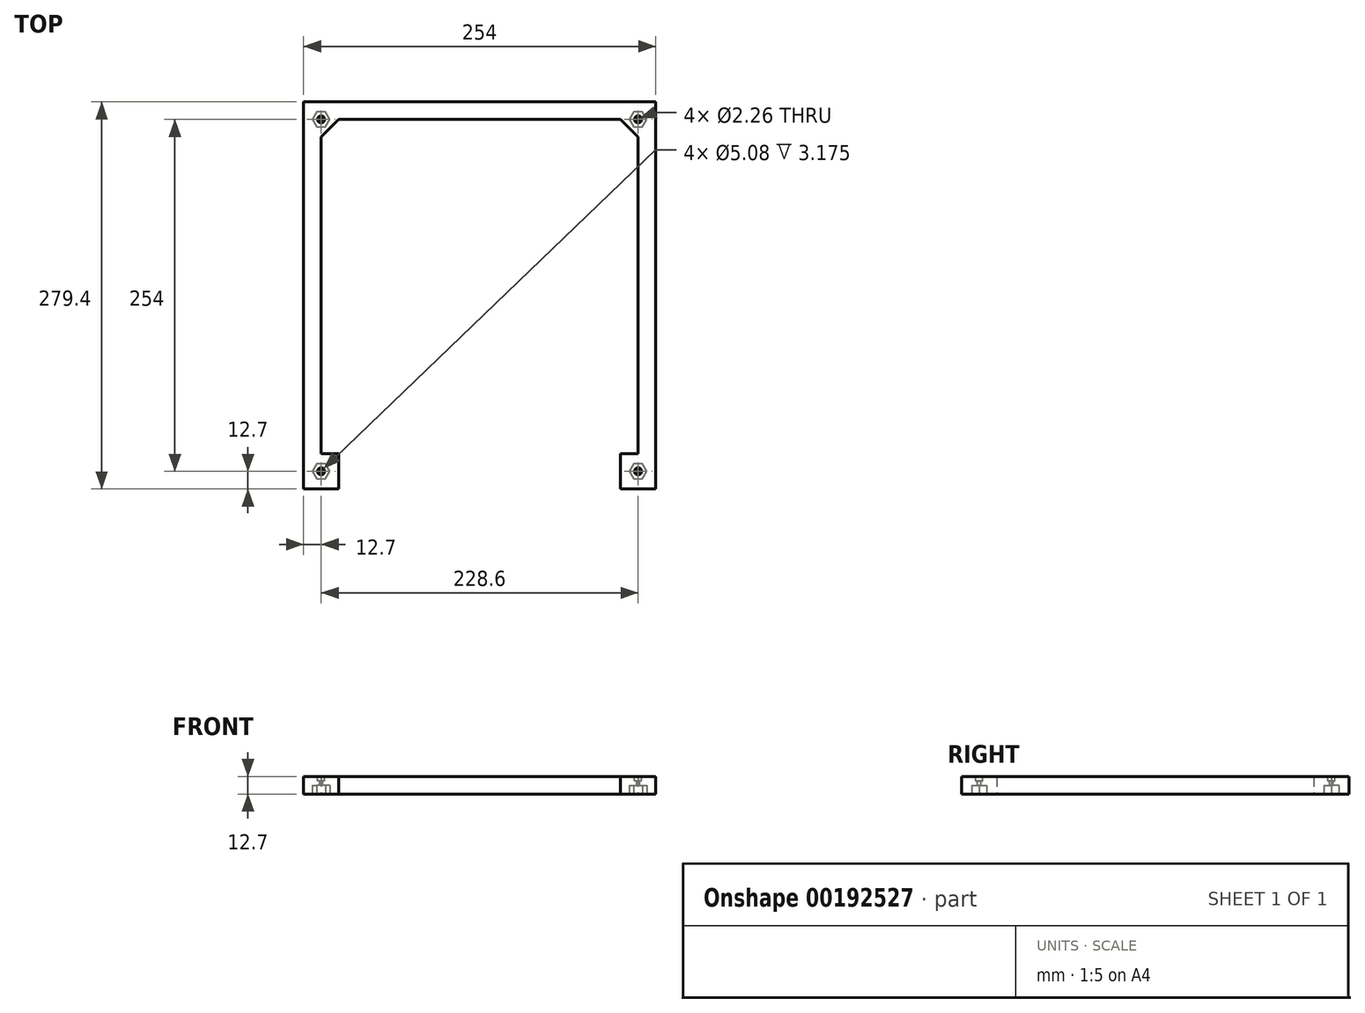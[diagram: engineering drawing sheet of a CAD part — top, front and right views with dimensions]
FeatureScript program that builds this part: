
annotation { "Feature Type Name" : "Feature", "Feature Type Description" : "" }
export const myFeature = defineFeature(function(context is Context, id is Id, definition is map)
    precondition{}
    {
        {
            var Q0;
            Q0=qCreatedBy(makeId("Top.planeOp"),FACE);
            var sketch = newSketch(context, id + "F0", { "sketchPlane" : qUnion([Q0])});
            skLineSegment(sketch, "E0.bottom", {"start": v(101.6, 127) * mm, "end": v(-101.6, 127) * mm});
            skLineSegment(sketch, "E0.left", {"start": v(114.3, 114.3) * mm, "end": v(114.3, -114.3) * mm});
            skLineSegment(sketch, "E0.right", {"start": v(-114.3, 114.3) * mm, "end": v(-114.3, -114.3) * mm});
            skPoint(sketch, "E0.middle", {"position": v(0, 0) * mm});
            skLineSegment(sketch, "E1.bottom", {"start": v(127, 139.7) * mm, "end": v(-127, 139.7) * mm});
            skLineSegment(sketch, "E1.top", {"start": v(127, -139.7) * mm, "end": v(114.3, -139.7) * mm});
            skLineSegment(sketch, "E1.left", {"start": v(127, 139.7) * mm, "end": v(127, -139.7) * mm});
            skLineSegment(sketch, "E1.right", {"start": v(-127, 139.7) * mm, "end": v(-127, -139.7) * mm});
            skLineSegment(sketch, "E2.trimOffspring", {"start": v(-114.3, -139.7) * mm, "end": v(-127, -139.7) * mm});
            skLineSegment(sketch, "E3.bottom", {"start": v(-127, 139.7) * mm, "end": v(-101.6, 139.7) * mm});
            skLineSegment(sketch, "E3.left", {"start": v(-127, 139.7) * mm, "end": v(-127, 114.3) * mm});
            skLineSegment(sketch, "E4.bottom", {"start": v(127, 139.7) * mm, "end": v(101.6, 139.7) * mm});
            skLineSegment(sketch, "E4.left", {"start": v(127, 139.7) * mm, "end": v(127, 114.3) * mm});
            skLineSegment(sketch, "E5.bottom", {"start": v(127, -139.7) * mm, "end": v(101.6, -139.7) * mm});
            skLineSegment(sketch, "E5.top", {"start": v(114.3, -114.3) * mm, "end": v(101.6, -114.3) * mm});
            skLineSegment(sketch, "E5.left", {"start": v(127, -139.7) * mm, "end": v(127, -114.3) * mm});
            skLineSegment(sketch, "E5.right", {"start": v(101.6, -139.7) * mm, "end": v(101.6, -114.3) * mm});
            skLineSegment(sketch, "E6.bottom", {"start": v(-127, -139.7) * mm, "end": v(-101.6, -139.7) * mm});
            skLineSegment(sketch, "E6.top", {"start": v(-114.3, -114.3) * mm, "end": v(-101.6, -114.3) * mm});
            skLineSegment(sketch, "E6.left", {"start": v(-127, -139.7) * mm, "end": v(-127, -114.3) * mm});
            skLineSegment(sketch, "E6.right", {"start": v(-101.6, -139.7) * mm, "end": v(-101.6, -114.3) * mm});
            skPoint(sketch, "E7.orphan", {"position": v(-114.3, 127) * mm});
            skPoint(sketch, "E8.start.orphan", {"position": v(-114.3, -127) * mm});
            skPoint(sketch, "E9.start.orphan", {"position": v(114.3, -127) * mm});
            skPoint(sketch, "E10.orphan", {"position": v(114.3, 127) * mm});
            skLineSegment(sketch, "E11", {"start": v(-114.3, 114.3) * mm, "end": v(-101.6, 127) * mm});
            skLineSegment(sketch, "E12", {"start": v(101.6, 127) * mm, "end": v(114.3, 114.3) * mm});
            skPoint(sketch, "E3.right.end.orphan", {"position": v(-101.6, 114.3) * mm});
            skPoint(sketch, "E4.top.end.orphan", {"position": v(101.6, 114.3) * mm});
            skSolve(sketch);
        }
        {
            var Q0;
            Q0 = qSketchRegion(id + "F0", true);
            extrude(context, id + "F1", {"entities" : qUnion([Q0]), "depth" : 12.7 * mm});
        }
        {
            var Q0;
            Q0=makeQuery(id+"F1.opExtrude","CAP_FACE",FACE,{"disambiguationData":[OSD([sQuery(id+"F0.wireOp",EDGE,"E0.bottom"),sQuery(id+"F0.wireOp",EDGE,"E0.left"),sQuery(id+"F0.wireOp",EDGE,"E0.right"),sQuery(id+"F0.wireOp",EDGE,"E1.bottom"),sQuery(id+"F0.wireOp",EDGE,"E1.left"),sQuery(id+"F0.wireOp",EDGE,"E1.right"),sQuery(id+"F0.wireOp",EDGE,"E3.bottom"),sQuery(id+"F0.wireOp",EDGE,"E3.top"),sQuery(id+"F0.wireOp",EDGE,"E3.left"),sQuery(id+"F0.wireOp",EDGE,"E3.right"),sQuery(id+"F0.wireOp",EDGE,"E4.bottom"),sQuery(id+"F0.wireOp",EDGE,"E4.top"),sQuery(id+"F0.wireOp",EDGE,"E4.left"),sQuery(id+"F0.wireOp",EDGE,"E4.right"),sQuery(id+"F0.wireOp",EDGE,"E5.bottom"),sQuery(id+"F0.wireOp",EDGE,"E5.top"),sQuery(id+"F0.wireOp",EDGE,"E5.left"),sQuery(id+"F0.wireOp",EDGE,"E5.right"),sQuery(id+"F0.wireOp",EDGE,"E6.bottom"),sQuery(id+"F0.wireOp",EDGE,"E6.top"),sQuery(id+"F0.wireOp",EDGE,"E6.left"),sQuery(id+"F0.wireOp",EDGE,"E6.right")])],"isStart":true});
            var sketch = newSketch(context, id + "F2", { "sketchPlane" : qUnion([Q0])});
            skSolve(sketch);
        }
        {
            var Q0;
            Q0=makeQuery(id+"F2.imprint","IMPRINT",FACE,{"disambiguationData":[TD([[makeQuery(id+"F2.imprint","IMPRINT",EDGE,{"derivedFrom":makeQuery(id+"F1.opExtrude","CAP_EDGE",EDGE,{"disambiguationData":[OSD([sQuery(id+"F0.wireOp",EDGE,"E0.bottom")])],"isStart":true})}),1.0]])]});
            var sketch = newSketch(context, id + "F3", { "sketchPlane" : qUnion([Q0])});
            skCircle(sketch, "E13.cCircle", {"center": v(-114.3, 127) * mm, "radius": 6.35 * mm, "construction": true});
            skLineSegment(sketch, "E13.0", {"start": v(-111.13, 121.5) * mm, "end": v(-117.48, 121.5) * mm});
            skLineSegment(sketch, "E13.1", {"start": v(-117.48, 121.5) * mm, "end": v(-120.65, 127) * mm});
            skLineSegment(sketch, "E13.2", {"start": v(-120.65, 127) * mm, "end": v(-117.48, 132.5) * mm});
            skLineSegment(sketch, "E13.3", {"start": v(-117.47, 132.5) * mm, "end": v(-111.12, 132.5) * mm});
            skLineSegment(sketch, "E13.4", {"start": v(-111.12, 132.5) * mm, "end": v(-107.95, 127) * mm});
            skLineSegment(sketch, "E13.5", {"start": v(-107.95, 127) * mm, "end": v(-111.13, 121.5) * mm});
            skCircle(sketch, "E14.cCircle", {"center": v(-114.3, -127) * mm, "radius": 6.35 * mm, "construction": true});
            skLineSegment(sketch, "E14.0", {"start": v(-111.12, -121.5) * mm, "end": v(-107.95, -127) * mm});
            skLineSegment(sketch, "E14.1", {"start": v(-107.95, -127) * mm, "end": v(-111.13, -132.5) * mm});
            skLineSegment(sketch, "E14.2", {"start": v(-111.13, -132.5) * mm, "end": v(-117.48, -132.5) * mm});
            skLineSegment(sketch, "E14.3", {"start": v(-117.48, -132.5) * mm, "end": v(-120.65, -127) * mm});
            skLineSegment(sketch, "E14.4", {"start": v(-120.65, -127) * mm, "end": v(-117.48, -121.5) * mm});
            skLineSegment(sketch, "E14.5", {"start": v(-117.48, -121.5) * mm, "end": v(-111.13, -121.5) * mm});
            skCircle(sketch, "E15.cCircle", {"center": v(114.3, -127) * mm, "radius": 6.35 * mm, "construction": true});
            skLineSegment(sketch, "E15.0", {"start": v(117.47, -121.5) * mm, "end": v(120.65, -127) * mm});
            skLineSegment(sketch, "E15.1", {"start": v(120.65, -127) * mm, "end": v(117.47, -132.5) * mm});
            skLineSegment(sketch, "E15.2", {"start": v(117.48, -132.5) * mm, "end": v(111.12, -132.5) * mm});
            skLineSegment(sketch, "E15.3", {"start": v(111.12, -132.5) * mm, "end": v(107.95, -127) * mm});
            skLineSegment(sketch, "E15.4", {"start": v(107.95, -127) * mm, "end": v(111.13, -121.5) * mm});
            skLineSegment(sketch, "E15.5", {"start": v(111.13, -121.5) * mm, "end": v(117.48, -121.5) * mm});
            skCircle(sketch, "E16.cCircle", {"center": v(114.3, 127) * mm, "radius": 6.35 * mm, "construction": true});
            skLineSegment(sketch, "E16.0", {"start": v(117.48, 132.5) * mm, "end": v(120.65, 127) * mm});
            skLineSegment(sketch, "E16.1", {"start": v(120.65, 127) * mm, "end": v(117.47, 121.5) * mm});
            skLineSegment(sketch, "E16.2", {"start": v(117.48, 121.5) * mm, "end": v(111.13, 121.5) * mm});
            skLineSegment(sketch, "E16.3", {"start": v(111.12, 121.5) * mm, "end": v(107.95, 127) * mm});
            skLineSegment(sketch, "E16.4", {"start": v(107.95, 127) * mm, "end": v(111.13, 132.5) * mm});
            skLineSegment(sketch, "E16.5", {"start": v(111.12, 132.5) * mm, "end": v(117.48, 132.5) * mm});
            skSolve(sketch);
        }
        {
            var Q0;
            Q0 = qSketchRegion(id + "F3", true);
            extrude(context, id + "F4", {"entities" : qUnion([Q0]), "operationType" : NewBodyOperationType.REMOVE, "oppositeDirection" : true, "depth" : 6.35 * mm});
        }
        {
            var Q0;
            Q0=makeQuery(id+"F1.opExtrude","CAP_FACE",FACE,{"disambiguationData":[OSD([sQuery(id+"F0.wireOp",EDGE,"E0.bottom"),sQuery(id+"F0.wireOp",EDGE,"E0.left"),sQuery(id+"F0.wireOp",EDGE,"E0.right"),sQuery(id+"F0.wireOp",EDGE,"E1.bottom"),sQuery(id+"F0.wireOp",EDGE,"E1.left"),sQuery(id+"F0.wireOp",EDGE,"E1.right"),sQuery(id+"F0.wireOp",EDGE,"E3.bottom"),sQuery(id+"F0.wireOp",EDGE,"E3.top"),sQuery(id+"F0.wireOp",EDGE,"E3.left"),sQuery(id+"F0.wireOp",EDGE,"E3.right"),sQuery(id+"F0.wireOp",EDGE,"E4.bottom"),sQuery(id+"F0.wireOp",EDGE,"E4.top"),sQuery(id+"F0.wireOp",EDGE,"E4.left"),sQuery(id+"F0.wireOp",EDGE,"E4.right"),sQuery(id+"F0.wireOp",EDGE,"E5.bottom"),sQuery(id+"F0.wireOp",EDGE,"E5.top"),sQuery(id+"F0.wireOp",EDGE,"E5.left"),sQuery(id+"F0.wireOp",EDGE,"E5.right"),sQuery(id+"F0.wireOp",EDGE,"E6.bottom"),sQuery(id+"F0.wireOp",EDGE,"E6.top"),sQuery(id+"F0.wireOp",EDGE,"E6.left"),sQuery(id+"F0.wireOp",EDGE,"E6.right")])],"isStart":false});
            var sketch = newSketch(context, id + "F5", { "sketchPlane" : qUnion([Q0])});
            skPoint(sketch, "E17", {"position": v(114.3, -127) * mm});
            skPoint(sketch, "E18", {"position": v(-114.3, -127) * mm});
            skPoint(sketch, "E19", {"position": v(-114.3, 127) * mm});
            skPoint(sketch, "E20", {"position": v(114.3, 127) * mm});
            skSolve(sketch);
        }
        {
            var Q0;
            Q0=sQuery(id+"F5.wireOp",VERTEX,"E19");
            var Q1;
            Q1=sQuery(id+"F5.wireOp",VERTEX,"E18");
            var Q2;
            Q2=sQuery(id+"F5.wireOp",VERTEX,"E17");
            var Q3;
            Q3=sQuery(id+"F5.wireOp",VERTEX,"E20");
            var Q4;
            Q4=makeQuery(id+"F1.opExtrude","SWEPT_BODY",BODY,{"disambiguationData":[OSD([sQuery(id+"F0.wireOp",EDGE,"E0.bottom"),sQuery(id+"F0.wireOp",EDGE,"E0.left"),sQuery(id+"F0.wireOp",EDGE,"E0.right"),sQuery(id+"F0.wireOp",EDGE,"E1.bottom"),sQuery(id+"F0.wireOp",EDGE,"E1.left"),sQuery(id+"F0.wireOp",EDGE,"E1.right"),sQuery(id+"F0.wireOp",EDGE,"E3.bottom"),sQuery(id+"F0.wireOp",EDGE,"E3.top"),sQuery(id+"F0.wireOp",EDGE,"E3.left"),sQuery(id+"F0.wireOp",EDGE,"E3.right"),sQuery(id+"F0.wireOp",EDGE,"E4.bottom"),sQuery(id+"F0.wireOp",EDGE,"E4.top"),sQuery(id+"F0.wireOp",EDGE,"E4.left"),sQuery(id+"F0.wireOp",EDGE,"E4.right"),sQuery(id+"F0.wireOp",EDGE,"E5.bottom"),sQuery(id+"F0.wireOp",EDGE,"E5.top"),sQuery(id+"F0.wireOp",EDGE,"E5.left"),sQuery(id+"F0.wireOp",EDGE,"E5.right"),sQuery(id+"F0.wireOp",EDGE,"E6.bottom"),sQuery(id+"F0.wireOp",EDGE,"E6.top"),sQuery(id+"F0.wireOp",EDGE,"E6.left"),sQuery(id+"F0.wireOp",EDGE,"E6.right")])]});
            hole(context, id + "F6", {"style" : HoleStyle.SIMPLE, "endStyle" : HoleEndStyle.BLIND, "standardTappedOrClearance" : lookupTablePath({ "standard" : "ANSI", "engagement" : "75%", "pitch" : "40 tpi", "size" : "#4", "type" : "Tapped" }), "standardBlindInLast" : lookupTablePath({ "standard" : "ANSI", "engagement" : "75%", "pitch" : "40 tpi", "size" : "#4", "type" : "Tapped" }), "holeDiameter" : 2.26 * mm, "holeDepth" : 12.7 * mm, "startFromSketch" : true, "locations" : qUnion([Q0, Q1, Q2, Q3]), "scope" : qUnion([Q4]), "majorDiameter" : 2.84 * mm});
        }
        {
            var Q0;
            Q0=makeQuery(id+"F1.opExtrude","CAP_FACE",FACE,{"disambiguationData":[OSD([sQuery(id+"F0.wireOp",EDGE,"E0.bottom"),sQuery(id+"F0.wireOp",EDGE,"E0.left"),sQuery(id+"F0.wireOp",EDGE,"E0.right"),sQuery(id+"F0.wireOp",EDGE,"E1.bottom"),sQuery(id+"F0.wireOp",EDGE,"E1.left"),sQuery(id+"F0.wireOp",EDGE,"E1.right"),sQuery(id+"F0.wireOp",EDGE,"E3.bottom"),sQuery(id+"F0.wireOp",EDGE,"E3.top"),sQuery(id+"F0.wireOp",EDGE,"E3.left"),sQuery(id+"F0.wireOp",EDGE,"E3.right"),sQuery(id+"F0.wireOp",EDGE,"E4.bottom"),sQuery(id+"F0.wireOp",EDGE,"E4.top"),sQuery(id+"F0.wireOp",EDGE,"E4.left"),sQuery(id+"F0.wireOp",EDGE,"E4.right"),sQuery(id+"F0.wireOp",EDGE,"E5.bottom"),sQuery(id+"F0.wireOp",EDGE,"E5.top"),sQuery(id+"F0.wireOp",EDGE,"E5.left"),sQuery(id+"F0.wireOp",EDGE,"E5.right"),sQuery(id+"F0.wireOp",EDGE,"E6.bottom"),sQuery(id+"F0.wireOp",EDGE,"E6.top"),sQuery(id+"F0.wireOp",EDGE,"E6.left"),sQuery(id+"F0.wireOp",EDGE,"E6.right")])],"isStart":false});
            var sketch = newSketch(context, id + "F7", { "sketchPlane" : qUnion([Q0])});
            skCircle(sketch, "E21", {"center": v(-114.3, 127) * mm, "radius": 2.54 * mm});
            skCircle(sketch, "E22", {"center": v(114.3, 127) * mm, "radius": 2.54 * mm});
            skCircle(sketch, "E23", {"center": v(114.3, -127) * mm, "radius": 2.54 * mm});
            skCircle(sketch, "E24", {"center": v(-114.3, -127) * mm, "radius": 2.54 * mm});
            skSolve(sketch);
        }
        {
            var Q0;
            Q0 = qSketchRegion(id + "F7", true);
            extrude(context, id + "F8", {"entities" : qUnion([Q0]), "operationType" : NewBodyOperationType.REMOVE, "oppositeDirection" : true, "depth" : 3.17 * mm});
        }
    });
